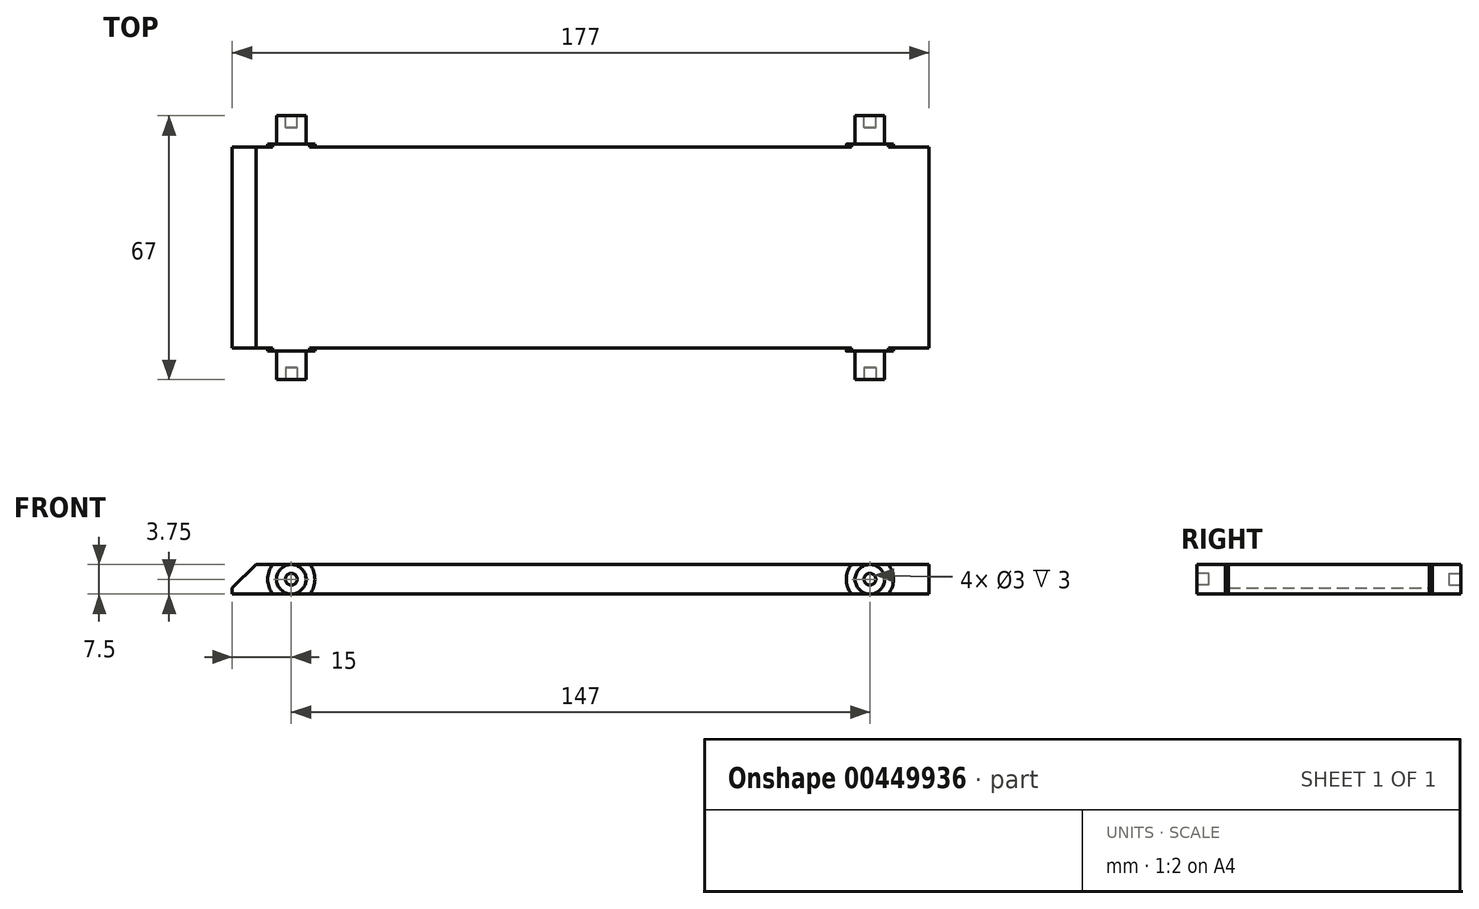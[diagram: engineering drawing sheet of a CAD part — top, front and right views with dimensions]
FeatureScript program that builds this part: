
annotation { "Feature Type Name" : "Feature", "Feature Type Description" : "" }
export const myFeature = defineFeature(function(context is Context, id is Id, definition is map)
    precondition{}
    {
        {
            var Q0;
            Q0=qCreatedBy(makeId("Top.planeOp"),FACE);
            var sketch = newSketch(context, id + "F0", { "sketchPlane" : qUnion([Q0])});
            skLineSegment(sketch, "E0.bottom", {"start": v(-88.5, 34.5) * mm, "end": v(88.5, 34.5) * mm, "construction": true});
            skLineSegment(sketch, "E0.top", {"start": v(-88.5, -34.5) * mm, "end": v(88.5, -34.5) * mm, "construction": true});
            skLineSegment(sketch, "E0.left", {"start": v(-88.5, 34.5) * mm, "end": v(-88.5, -34.5) * mm, "construction": true});
            skLineSegment(sketch, "E0.right", {"start": v(88.5, 34.5) * mm, "end": v(88.5, -34.5) * mm, "construction": true});
            skPoint(sketch, "E1", {"position": v(88.5, 0) * mm});
            skPoint(sketch, "E2", {"position": v(0, -34.5) * mm});
            skLineSegment(sketch, "E3.bottom", {"start": v(-88.5, 34.5) * mm, "end": v(-58.5, 34.5) * mm, "construction": true});
            skLineSegment(sketch, "E3.top", {"start": v(-88.5, 25.5) * mm, "end": v(-58.5, 25.5) * mm, "construction": true});
            skLineSegment(sketch, "E3.left", {"start": v(-88.5, 34.5) * mm, "end": v(-88.5, 25.5) * mm, "construction": true});
            skLineSegment(sketch, "E3.right", {"start": v(-58.5, 34.5) * mm, "end": v(-58.5, 25.5) * mm, "construction": true});
            skLineSegment(sketch, "E4.bottom", {"start": v(-88.5, -34.5) * mm, "end": v(-58.5, -34.5) * mm, "construction": true});
            skLineSegment(sketch, "E4.top", {"start": v(-88.5, -25.5) * mm, "end": v(-58.5, -25.5) * mm, "construction": true});
            skLineSegment(sketch, "E4.left", {"start": v(-88.5, -34.5) * mm, "end": v(-88.5, -25.5) * mm, "construction": true});
            skLineSegment(sketch, "E4.right", {"start": v(-58.5, -34.5) * mm, "end": v(-58.5, -25.5) * mm, "construction": true});
            skLineSegment(sketch, "E5.bottom", {"start": v(88.5, 34.5) * mm, "end": v(58.5, 34.5) * mm, "construction": true});
            skLineSegment(sketch, "E5.top", {"start": v(88.5, 25.5) * mm, "end": v(58.5, 25.5) * mm, "construction": true});
            skLineSegment(sketch, "E5.left", {"start": v(88.5, 34.5) * mm, "end": v(88.5, 25.5) * mm, "construction": true});
            skLineSegment(sketch, "E5.right", {"start": v(58.5, 34.5) * mm, "end": v(58.5, 25.5) * mm, "construction": true});
            skLineSegment(sketch, "E6.bottom", {"start": v(88.5, -34.5) * mm, "end": v(58.5, -34.5) * mm, "construction": true});
            skLineSegment(sketch, "E6.top", {"start": v(88.5, -25.5) * mm, "end": v(58.5, -25.5) * mm, "construction": true});
            skLineSegment(sketch, "E6.left", {"start": v(88.5, -34.5) * mm, "end": v(88.5, -25.5) * mm, "construction": true});
            skLineSegment(sketch, "E6.right", {"start": v(58.5, -34.5) * mm, "end": v(58.5, -25.5) * mm, "construction": true});
            skLineSegment(sketch, "E7.bottom", {"start": v(-88.5, 25.5) * mm, "end": v(88.5, 25.5) * mm});
            skLineSegment(sketch, "E7.top", {"start": v(-88.5, -25.5) * mm, "end": v(88.5, -25.5) * mm});
            skLineSegment(sketch, "E7.left", {"start": v(-88.5, 25.5) * mm, "end": v(-88.5, -25.5) * mm});
            skLineSegment(sketch, "E7.right", {"start": v(88.5, 25.5) * mm, "end": v(88.5, -25.5) * mm});
            skPoint(sketch, "E8", {"position": v(-73.5, 34.5) * mm});
            skPoint(sketch, "E9", {"position": v(-73.5, -34.5) * mm});
            skPoint(sketch, "E10", {"position": v(73.5, -34.5) * mm});
            skPoint(sketch, "E11", {"position": v(73.5, 34.5) * mm});
            skSolve(sketch);
        }
        {
            var Q0;
            Q0=makeQuery(id+"F0.imprint","IMPRINT",FACE,{"disambiguationData":[TD([[makeQuery(id+"F0.imprint","IMPRINT",EDGE,{"derivedFrom":sQuery(id+"F0.wireOp",EDGE,"E7.bottom")}),-1.0]])]});
            extrude(context, id + "F1", {"entities" : qUnion([Q0]), "depth" : 7.5 * mm});
        }
        {
            var Q0;
            Q0=makeQuery(id+"F1.opExtrude","SWEPT_FACE",FACE,{"disambiguationData":[OSD([sQuery(id+"F0.wireOp",EDGE,"E7.top")])]});
            var sketch = newSketch(context, id + "F2", { "sketchPlane" : qUnion([Q0])});
            skPoint(sketch, "E12.0", {"position": v(-73.5, 0) * mm});
            skPoint(sketch, "E13.0", {"position": v(73.5, 0) * mm});
            skPoint(sketch, "E14", {"position": v(-88.5, 3.75) * mm});
            skCircle(sketch, "E15", {"center": v(-73.5, 3.75) * mm, "radius": 3.75 * mm});
            skPoint(sketch, "E16", {"position": v(88.5, 3.75) * mm});
            skCircle(sketch, "E17", {"center": v(73.5, 3.75) * mm, "radius": 3.75 * mm});
            skCircle(sketch, "E18", {"center": v(-73.5, 3.75) * mm, "radius": 6 * mm});
            skCircle(sketch, "E19", {"center": v(73.5, 3.75) * mm, "radius": 6 * mm});
            skSolve(sketch);
        }
        {
            var Q0;
            {var subQ0=sQuery(id+"F2.wireOp",EDGE,"E17");var subQ1=sQuery(id+"F0.wireOp",EDGE,"E7.top");var subQ2=makeQuery(id+"F2.imprint","INTERSECT",VERTEX,{"derivedFrom":[makeQuery(id+"F1.opExtrude","CAP_EDGE",EDGE,{"disambiguationData":[OSD([subQ1])],"isStart":false}),subQ0]});Q0=makeQuery(id+"F2.imprint","IMPRINT",FACE,{"disambiguationData":[TD([[makeQuery(id+"F2.imprint","IMPRINT",EDGE,{"disambiguationData":[TD([[subQ2,-1.0]])],"derivedFrom":subQ0}),1.0]])]});}
            var Q1;
            {var subQ0=sQuery(id+"F2.wireOp",EDGE,"E15");var subQ1=sQuery(id+"F0.wireOp",EDGE,"E7.top");var subQ2=makeQuery(id+"F2.imprint","INTERSECT",VERTEX,{"derivedFrom":[makeQuery(id+"F1.opExtrude","CAP_EDGE",EDGE,{"disambiguationData":[OSD([subQ1])],"isStart":false}),subQ0]});Q1=makeQuery(id+"F2.imprint","IMPRINT",FACE,{"disambiguationData":[TD([[makeQuery(id+"F2.imprint","IMPRINT",EDGE,{"disambiguationData":[TD([[subQ2,-1.0]])],"derivedFrom":subQ0}),1.0]])]});}
            extrude(context, id + "F3", {"entities" : qUnion([Q0, Q1]), "operationType" : NewBodyOperationType.ADD, "depth" : 8 * mm});
        }
        {
            var Q0;
            {var subQ0=sQuery(id+"F2.wireOp",EDGE,"E15");var subQ1=sQuery(id+"F0.wireOp",EDGE,"E7.top");var subQ2=makeQuery(id+"F1.opExtrude","CAP_EDGE",EDGE,{"disambiguationData":[OSD([subQ1])],"isStart":false});var subQ3=makeQuery(id+"F2.imprint","INTERSECT",VERTEX,{"derivedFrom":[subQ2,subQ0]});Q0=makeQuery(id+"F2.imprint","IMPRINT",FACE,{"disambiguationData":[TD([[makeQuery(id+"F2.imprint","IMPRINT",EDGE,{"disambiguationData":[TD([[subQ3,-1.0]])],"derivedFrom":subQ0}),-1.0]])]});}
            var Q1;
            {var subQ0=sQuery(id+"F2.wireOp",EDGE,"E15");var subQ1=sQuery(id+"F0.wireOp",EDGE,"E7.top");var subQ2=makeQuery(id+"F1.opExtrude","CAP_EDGE",EDGE,{"disambiguationData":[OSD([subQ1])],"isStart":false});var subQ3=makeQuery(id+"F2.imprint","INTERSECT",VERTEX,{"derivedFrom":[subQ2,subQ0]});Q1=makeQuery(id+"F2.imprint","IMPRINT",FACE,{"disambiguationData":[TD([[makeQuery(id+"F2.imprint","IMPRINT",EDGE,{"disambiguationData":[TD([[subQ3,1.0]])],"derivedFrom":subQ0}),-1.0]])]});}
            var Q2;
            {var subQ0=sQuery(id+"F2.wireOp",EDGE,"E17");var subQ1=sQuery(id+"F0.wireOp",EDGE,"E7.top");var subQ2=makeQuery(id+"F1.opExtrude","CAP_EDGE",EDGE,{"disambiguationData":[OSD([subQ1])],"isStart":false});var subQ3=makeQuery(id+"F2.imprint","INTERSECT",VERTEX,{"derivedFrom":[subQ2,subQ0]});Q2=makeQuery(id+"F2.imprint","IMPRINT",FACE,{"disambiguationData":[TD([[makeQuery(id+"F2.imprint","IMPRINT",EDGE,{"disambiguationData":[TD([[subQ3,1.0]])],"derivedFrom":subQ0}),-1.0]])]});}
            var Q3;
            {var subQ0=sQuery(id+"F2.wireOp",EDGE,"E17");var subQ1=sQuery(id+"F0.wireOp",EDGE,"E7.top");var subQ2=makeQuery(id+"F1.opExtrude","CAP_EDGE",EDGE,{"disambiguationData":[OSD([subQ1])],"isStart":false});var subQ3=makeQuery(id+"F2.imprint","INTERSECT",VERTEX,{"derivedFrom":[subQ2,subQ0]});Q3=makeQuery(id+"F2.imprint","IMPRINT",FACE,{"disambiguationData":[TD([[makeQuery(id+"F2.imprint","IMPRINT",EDGE,{"disambiguationData":[TD([[subQ3,-1.0]])],"derivedFrom":subQ0}),-1.0]])]});}
            extrude(context, id + "F4", {"entities" : qUnion([Q0, Q1, Q2, Q3]), "operationType" : NewBodyOperationType.ADD, "depth" : .8 * mm});
        }
        {
            var Q0;
            Q0=makeQuery(id+"F3.opExtrude","CAP_FACE",FACE,{"disambiguationData":[OSD([sQuery(id+"F2.wireOp",EDGE,"E15")])],"isStart":false});
            var sketch = newSketch(context, id + "F5", { "sketchPlane" : qUnion([Q0])});
            skCircle(sketch, "E20", {"center": v(-73.5, 3.75) * mm, "radius": 1.5 * mm});
            skPoint(sketch, "E21.0", {"position": v(73.5, 3.75) * mm});
            skCircle(sketch, "E22", {"center": v(73.5, 3.75) * mm, "radius": 1.5 * mm});
            skSolve(sketch);
        }
        {
            var Q0;
            Q0=makeQuery(id+"F5.imprint","IMPRINT",FACE,{"disambiguationData":[TD([[makeQuery(id+"F5.imprint","IMPRINT",EDGE,{"derivedFrom":sQuery(id+"F5.wireOp",EDGE,"E20")}),1.0]])]});
            var Q1;
            Q1=makeQuery(id+"F5.imprint","IMPRINT",FACE,{"disambiguationData":[TD([[makeQuery(id+"F5.imprint","IMPRINT",EDGE,{"derivedFrom":sQuery(id+"F5.wireOp",EDGE,"E22")}),1.0]])]});
            extrude(context, id + "F6", {"entities" : qUnion([Q0, Q1]), "operationType" : NewBodyOperationType.REMOVE, "oppositeDirection" : true, "depth" : 3 * mm});
        }
        {
            var Q0;
            Q0=makeQuery(id+"F1.opExtrude","SWEPT_FACE",FACE,{"disambiguationData":[OSD([sQuery(id+"F0.wireOp",EDGE,"E7.bottom")])]});
            var sketch = newSketch(context, id + "F7", { "sketchPlane" : qUnion([Q0])});
            skPoint(sketch, "E23.0", {"position": v(-73.5, 0) * mm});
            skPoint(sketch, "E24.0", {"position": v(73.5, 0) * mm});
            skPoint(sketch, "E25", {"position": v(-88.5, 3.75) * mm});
            skCircle(sketch, "E26", {"center": v(-73.5, 3.75) * mm, "radius": 3.75 * mm});
            skCircle(sketch, "E27", {"center": v(-73.5, 3.75) * mm, "radius": 6 * mm});
            skPoint(sketch, "E28", {"position": v(88.5, 3.75) * mm});
            skCircle(sketch, "E29", {"center": v(73.5, 3.75) * mm, "radius": 3.75 * mm});
            skCircle(sketch, "E30", {"center": v(73.5, 3.75) * mm, "radius": 6 * mm});
            skLineSegment(sketch, "E31", {"start": v(-78.18, 0) * mm, "end": v(-68.82, 0) * mm});
            skLineSegment(sketch, "E32", {"start": v(-78.18, 7.5) * mm, "end": v(-68.82, 7.5) * mm});
            skLineSegment(sketch, "E33", {"start": v(68.82, 7.5) * mm, "end": v(78.18, 7.5) * mm});
            skLineSegment(sketch, "E34", {"start": v(78.18, 0) * mm, "end": v(68.82, 0) * mm});
            skSolve(sketch);
        }
        {
            var Q0;
            {var subQ0=sQuery(id+"F7.wireOp",EDGE,"E29");var subQ1=sQuery(id+"F0.wireOp",EDGE,"E7.bottom");var subQ2=makeQuery(id+"F7.imprint","INTERSECT",VERTEX,{"derivedFrom":[makeQuery(id+"F1.opExtrude","CAP_EDGE",EDGE,{"disambiguationData":[OSD([subQ1])],"isStart":false}),subQ0]});Q0=makeQuery(id+"F7.imprint","IMPRINT",FACE,{"disambiguationData":[TD([[makeQuery(id+"F7.imprint","IMPRINT",EDGE,{"disambiguationData":[TD([[subQ2,-1.0]])],"derivedFrom":subQ0}),1.0]])]});}
            var Q1;
            {var subQ0=sQuery(id+"F7.wireOp",EDGE,"E26");var subQ1=sQuery(id+"F0.wireOp",EDGE,"E7.bottom");var subQ2=makeQuery(id+"F7.imprint","INTERSECT",VERTEX,{"derivedFrom":[makeQuery(id+"F1.opExtrude","CAP_EDGE",EDGE,{"disambiguationData":[OSD([subQ1])],"isStart":false}),subQ0]});Q1=makeQuery(id+"F7.imprint","IMPRINT",FACE,{"disambiguationData":[TD([[makeQuery(id+"F7.imprint","IMPRINT",EDGE,{"disambiguationData":[TD([[subQ2,-1.0]])],"derivedFrom":subQ0}),1.0]])]});}
            extrude(context, id + "F8", {"entities" : qUnion([Q0, Q1]), "operationType" : NewBodyOperationType.ADD, "depth" : 8 * mm});
        }
        {
            var Q0;
            {var subQ0=sQuery(id+"F7.wireOp",EDGE,"E33");var subQ1=sQuery(id+"F7.wireOp",EDGE,"E29");var subQ2=makeQuery(id+"F7.imprint","INTERSECT",VERTEX,{"derivedFrom":[subQ1,subQ0]});Q0=makeQuery(id+"F7.imprint","IMPRINT",FACE,{"disambiguationData":[TD([[makeQuery(id+"F7.imprint","IMPRINT",EDGE,{"disambiguationData":[TD([[subQ2,-1.0]])],"derivedFrom":subQ1}),-1.0]])]});}
            var Q1;
            {var subQ0=sQuery(id+"F7.wireOp",EDGE,"E33");var subQ1=sQuery(id+"F7.wireOp",EDGE,"E29");var subQ2=makeQuery(id+"F7.imprint","INTERSECT",VERTEX,{"derivedFrom":[subQ1,subQ0]});Q1=makeQuery(id+"F7.imprint","IMPRINT",FACE,{"disambiguationData":[TD([[makeQuery(id+"F7.imprint","IMPRINT",EDGE,{"disambiguationData":[TD([[subQ2,1.0]])],"derivedFrom":subQ1}),-1.0]])]});}
            var Q2;
            {var subQ0=sQuery(id+"F7.wireOp",EDGE,"E31");var subQ1=sQuery(id+"F7.wireOp",EDGE,"E26");var subQ2=makeQuery(id+"F7.imprint","INTERSECT",VERTEX,{"derivedFrom":[subQ1,subQ0]});Q2=makeQuery(id+"F7.imprint","IMPRINT",FACE,{"disambiguationData":[TD([[makeQuery(id+"F7.imprint","IMPRINT",EDGE,{"disambiguationData":[TD([[subQ2,1.0]])],"derivedFrom":subQ1}),-1.0]])]});}
            var Q3;
            {var subQ0=sQuery(id+"F7.wireOp",EDGE,"E31");var subQ1=sQuery(id+"F7.wireOp",EDGE,"E26");var subQ2=makeQuery(id+"F7.imprint","INTERSECT",VERTEX,{"derivedFrom":[subQ1,subQ0]});Q3=makeQuery(id+"F7.imprint","IMPRINT",FACE,{"disambiguationData":[TD([[makeQuery(id+"F7.imprint","IMPRINT",EDGE,{"disambiguationData":[TD([[subQ2,-1.0]])],"derivedFrom":subQ1}),-1.0]])]});}
            extrude(context, id + "F9", {"entities" : qUnion([Q0, Q1, Q2, Q3]), "operationType" : NewBodyOperationType.ADD, "depth" : .8 * mm});
        }
        {
            var Q0;
            Q0=makeQuery(id+"F8.opExtrude","CAP_FACE",FACE,{"disambiguationData":[OSD([sQuery(id+"F7.wireOp",EDGE,"E26")])],"isStart":false});
            var sketch = newSketch(context, id + "F10", { "sketchPlane" : qUnion([Q0])});
            skPoint(sketch, "E35.0", {"position": v(-73.5, 3.75) * mm});
            skPoint(sketch, "E36.0", {"position": v(73.5, 3.75) * mm});
            skCircle(sketch, "E37", {"center": v(-73.5, 3.75) * mm, "radius": 1.5 * mm});
            skCircle(sketch, "E38", {"center": v(73.5, 3.75) * mm, "radius": 1.5 * mm});
            skSolve(sketch);
        }
        {
            var Q0;
            Q0=makeQuery(id+"F10.imprint","IMPRINT",FACE,{"disambiguationData":[TD([[makeQuery(id+"F10.imprint","IMPRINT",EDGE,{"derivedFrom":sQuery(id+"F10.wireOp",EDGE,"E37")}),1.0]])]});
            var Q1;
            Q1=makeQuery(id+"F10.imprint","IMPRINT",FACE,{"disambiguationData":[TD([[makeQuery(id+"F10.imprint","IMPRINT",EDGE,{"derivedFrom":sQuery(id+"F10.wireOp",EDGE,"E38")}),1.0]])]});
            extrude(context, id + "F11", {"entities" : qUnion([Q0, Q1]), "operationType" : NewBodyOperationType.REMOVE, "oppositeDirection" : true, "depth" : 3 * mm});
        }
        {
            var Q0;
            Q0=makeQuery(id+"F1.opExtrude","CAP_EDGE",EDGE,{"disambiguationData":[OSD([sQuery(id+"F0.wireOp",EDGE,"E7.left")])],"isStart":false});
            chamfer(context, id + "F12", {"entities" : qUnion([Q0]), "width" : 6 * mm, "tangentPropagation" : true});
        }
    });
